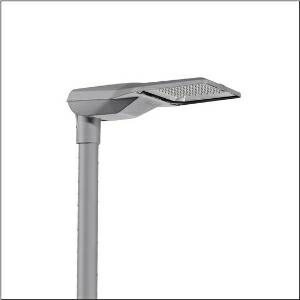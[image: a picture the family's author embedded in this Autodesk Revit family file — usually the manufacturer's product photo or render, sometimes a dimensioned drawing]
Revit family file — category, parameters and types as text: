
# Revit family: streetlight_sl_21_iq_midi___stw1_0a_5xe3e41d08mb_aeb4
name_source: partatom
category: Lighting Fixtures
units: mm (PartAtom-declared; Revit-internal decimal feet)

## family parameters
Cut with Voids When Loaded = No
Host = Face
Light Source = No
Part Type = Normal
Room Calculation Point = No
Round Connector Dimension = Use Diameter
Shared = No

## types (1)
- --- (1 x LED, 20360 lm, 146.7 W, 4000K)
    Apparent Load = 147 VA
    CIE Flux Codes = 38 75 98 100 100
    Color Rendering = 70
    Color Temperature = 4000K
    Default Elevation = 1800 mm
    Description = Streetlight SL 21 iQ midi, mast luminaire, primary light control with lens, of PMMA, primary optical cover: cover, of toughened safety glass, transparent, light distribution: STW1.0a, light emission: direct distribution, primary light characteristic: asymmetric, installation type: post-top, side-entry, LED, High Power LED, rated luminous flux: 20.360lm, luminous efficacy: 139lm/W, light colour: 740, colour temperature: 4000K, control gear: iQ-Comfort, control: Auto-Match, Temp-Guard, Lumen-Switch, Night-Set, Smart-Wire, Light-Fading, Desk-Remote (wireless, voltage-free reading and setting of iQ features in the workshop via application-optimized NFC function/RFID function), optimised constant luminous flux control (CLO 2.0), pre-setting: linear dimming characteristic, mains connection: 230..240V, AC, 50/60Hz, start of lifetime: 147W, end of service life: 161W, reduction: 62W, luminaire housing, of diecast aluminium, powder-coated, Siteco® metallic grey (DB 702S), corrosivity category C5 mid according to DIN EN ISO 12944, please order mast flange separately, inclination adjustable: 0°, 5°, 10°, 15°, sealing non-destructively replaceable, multi-level sealing system, length: 644mm, width: 335mm, height: 110mm, mast flange for spigot size: 42mm (side-entry): 5XC10008XM4, 60/48mm (side-entry/post-top): 5XC10108XM2, 76/60mm (side-entry/post-top): 5XC10108XM1, mounting height: 4..8m, protection rating (complete): IP66, insulation class (complete): insulation class II (safety insulation), certification: CE, ENEC, ENEC+, VDE, impact resistance: IK10, permissible operating ambient temperature for outdoor applications: -40..+50°C, standard-compliant lighting for roads and squares, packaging unit: 1 piece

Light Distribution: STW1.0a
    Height = 111 mm
    Lamp = 1 x LED
    Lamp Light Flux = 20360 lm
    Lamp Power = 146.7 W
    Lamp count = 1
    Length = 644 mm
    Luminous efficacy = 139 lm/W
    Manufacturer = Siteco
    ModVariant = No
    Model = 5XE3E41D08MB
    Number of Poles = 1
    OnlyDefault = Yes
    Power Factor = 1
    Product Name = Streetlight SL 21 iQ midi | STW1.0a
    Product group = mast luminaire | pylon top
    ProductGroupID = 6100
    Protection Class = Protection class II
    Protection Degree = IP 66
    RLX_Detail_Level = 1
    RLX_Emergency_Light_Flux = 0 lm
    RLX_Emergency_Type = 0
    RLX_Emergency_Type_DB = No
    RlxData = <blob elided: 26949 chars, md5=ec69c793>
    Socket = socket
    Standby Power = 0 W
    System Light Flux = 20360 lm
    System Power = 147 W
    Type Comments = factory setting: luminous flux: 100 % | dim-lin: 254 | 753 mA
    Type Image = l_1004298.jpg
    URL = http://relux.com
    VarID = @adj_209361
    Voltage = 0 V
    Weight = 0.00 kg
    Width = 336 mm

## geometry (parser evidence)
native form markers: Blend x4, Sweep x13
no freeform markers — native parametric forms only
